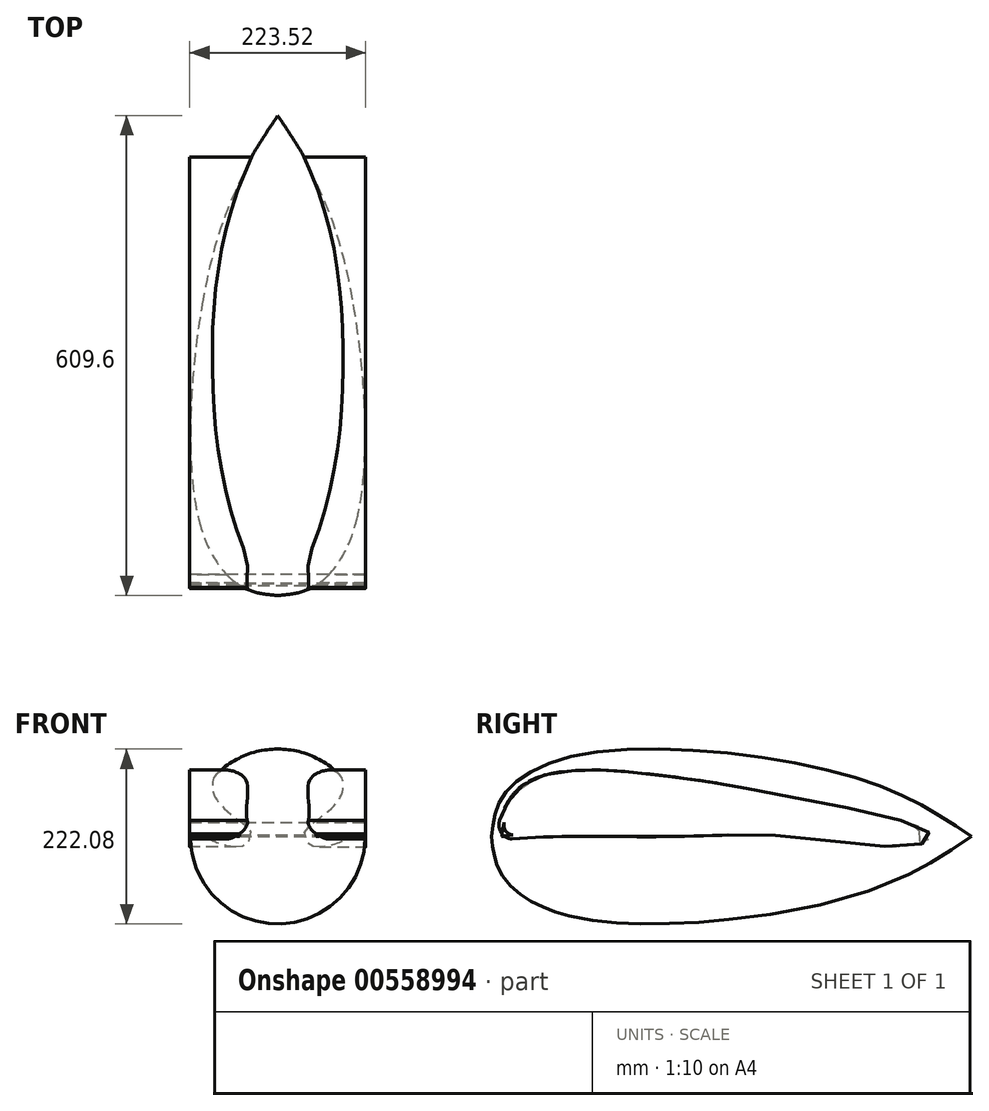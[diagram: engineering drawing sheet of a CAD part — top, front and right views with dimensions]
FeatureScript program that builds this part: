
annotation { "Feature Type Name" : "Feature", "Feature Type Description" : "" }
export const myFeature = defineFeature(function(context is Context, id is Id, definition is map)
    precondition{}
    {
        {
            var Q0;
            Q0=qCreatedBy(makeId("Right.planeOp"),FACE);
            var sketch = newSketch(context, id + "F0", { "sketchPlane" : qUnion([Q0])});
            skLineSegment(sketch, "E0", {"start": v(0, 0) * mm, "end": v(609.6, 0) * mm});
            skPoint(sketch, "E1", {"position": v(101.6, 101.6) * mm});
            skPoint(sketch, "E2", {"position": v(457.2, 76.2) * mm});
            skPoint(sketch, "E3", {"position": v(10.7, 44.9) * mm});
            skFitSpline(sketch, "E4", {"points": [v(0, 0) * mm, v(10.7, 44.9) * mm, v(101.6, 101.6) * mm, v(457.2, 76.2) * mm, v(609.6, 0) * mm], "startDerivative": vector(27.37, 324.9) * mm, "endDerivative": vector(463.18, -311.95) * mm});
            skSolve(sketch);
        }
        {
            var Q0;
            Q0=makeQuery(id+"F0.imprint","IMPRINT",FACE,{"disambiguationData":[TD([[makeQuery(id+"F0.imprint","IMPRINT",EDGE,{"derivedFrom":sQuery(id+"F0.wireOp",EDGE,"E0")}),1.0]])]});
            var Q1;
            Q1=sQuery(id+"F0.wireOp",EDGE,"E0");
            revolve(context, id + "F1", {"entities" : qUnion([Q0]), "axis" : qUnion([Q1]), "revolveType" : RevolveType.FULL});
        }
        {
            var Q0;
            Q0=qCreatedBy(makeId("Right.planeOp"),FACE);
            cPlane(context, id + "F2", {"entities" : qUnion([Q0]), "cplaneType" : CPlaneType.OFFSET, "offset" : 111.76 * mm, "width" : 152.4 * mm, "height" : 152.4 * mm});
        }
        {
            var Q0;
            Q0=qCreatedBy(makeId("Right.planeOp"),FACE);
            var sketch = newSketch(context, id + "F3", { "sketchPlane" : qUnion([Q0])});
            skArc(sketch, "E5", {"start": v(10.02, 20.07) * mm, "mid": v(12.18, 4.48) * mm, "end": v(25.93, -3.17) * mm});
            skFitSpline(sketch, "E6", {"points": [v(10.02, 20.07) * mm, v(20.48, 43.93) * mm, v(41.84, 66.96) * mm, v(75.54, 79.94) * mm, v(123.06, 84.33) * mm, v(173.3, 82.03) * mm, v(273.76, 69.7) * mm, v(373.3, 51.58) * mm, v(542.31, 12.72) * mm, v(557.1, 0) * mm, v(536.68, -11.92) * mm, v(376.14, 0) * mm, v(240.25, 0) * mm, v(95.21, 0) * mm, v(25.93, -3.17) * mm], "startDerivative": vector(200.1, 556.1) * mm, "endDerivative": vector(-874.54, -58.98) * mm});
            skSolve(sketch);
        }
        {
            var Q0;
            Q0=qCreatedBy(id+"F2.planeOp",FACE);
            var sketch = newSketch(context, id + "F4", { "sketchPlane" : qUnion([Q0])});
            skPoint(sketch, "E7", {"position": v(12.7, 0) * mm});
            skPoint(sketch, "E8", {"position": v(88.9, 76.2) * mm});
            skPoint(sketch, "E9", {"position": v(393.7, 38.1) * mm});
            skPoint(sketch, "E10", {"position": v(546.1, 0) * mm});
            skPoint(sketch, "E11", {"position": v(393.7, 6.35) * mm});
            skFitSpline(sketch, "E12", {"points": [v(12.7, 0) * mm, v(88.9, 76.2) * mm, v(393.7, 38.1) * mm, v(546.1, 0) * mm, v(393.7, 6.35) * mm], "startDerivative": vector(81.46, 775.02) * mm, "endDerivative": vector(-965.3, 69.79) * mm});
            skFitSpline(sketch, "E13", {"points": [v(393.7, 6.35) * mm, v(12.7, 0) * mm], "startDerivative": vector(-151.2, 19.05) * mm, "endDerivative": vector(-291.33, -38.1) * mm});
            skLineSegment(sketch, "E14", {"start": v(12.7, 0) * mm, "end": v(18.04, 50.8) * mm});
            skLineSegment(sketch, "E15", {"start": v(12.7, 0) * mm, "end": v(12.7, 28.68) * mm});
            skLineSegment(sketch, "E16", {"start": v(343.3, 12.7) * mm, "end": v(393.7, 6.35) * mm});
            skLineSegment(sketch, "E17", {"start": v(393.7, 6.35) * mm, "end": v(393.7, 32.34) * mm});
            skLineSegment(sketch, "E18", {"start": v(109.81, 12.7) * mm, "end": v(12.7, 0) * mm});
            skArc(sketch, "E19.filletArc", {"start": v(15.73, 17.63) * mm, "mid": v(18.46, 6.24) * mm, "end": v(29.35, 1.92) * mm});
            skSolve(sketch);
        }
        {
            var Q0;
            Q0 = qSketchRegion(id + "F3", true);
            extrude(context, id + "F5", {"entities" : qUnion([Q0]), "operationType" : NewBodyOperationType.ADD, "endBound" : BoundingType.SYMMETRIC, "depth" : 223.52 * mm, "offsetDistance" : 25.4 * mm});
        }
        {
            var Q0;
            {var subQ0=sQuery(id+"F4.wireOp",EDGE,"E12");Q0=makeQuery(id+"F4.imprint","IMPRINT",FACE,{"disambiguationData":[TD([[makeQuery(id+"F4.imprint","IMPRINT",EDGE,{"derivedFrom":subQ0}),-1.0]])]});}
            extrude(context, id + "F6", {"entities" : qUnion([Q0]), "operationType" : NewBodyOperationType.REMOVE, "endBound" : BoundingType.SYMMETRIC, "oppositeDirection" : true, "depth" : 652.27 * mm, "offsetDistance" : 25.4 * mm});
        }
    });
